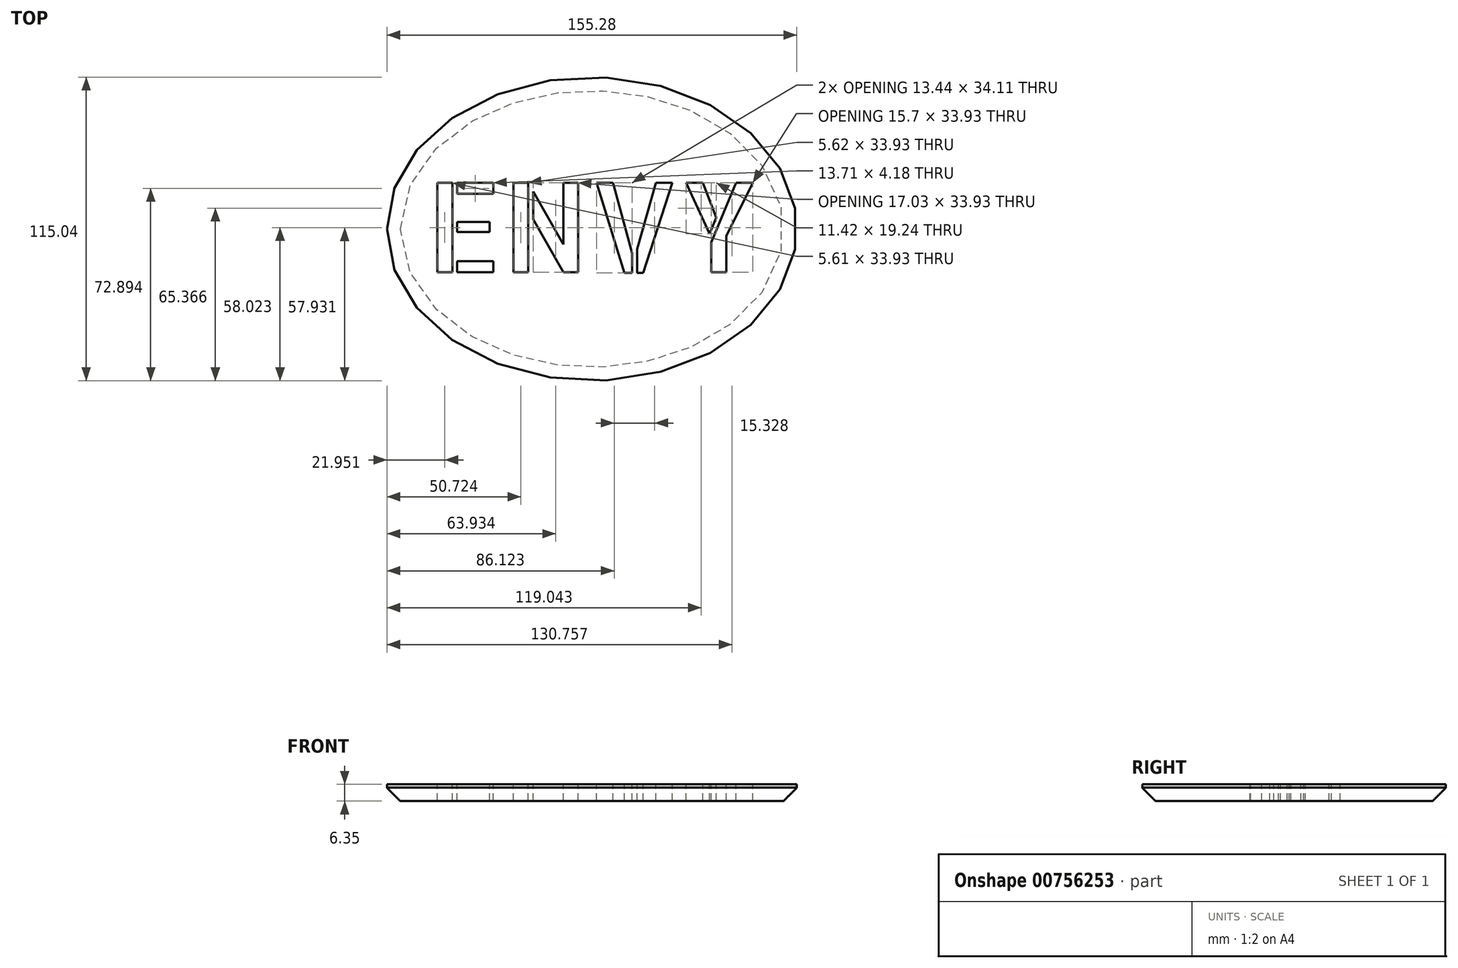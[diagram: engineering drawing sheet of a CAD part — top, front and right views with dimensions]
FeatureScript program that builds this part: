
annotation { "Feature Type Name" : "Feature", "Feature Type Description" : "" }
export const myFeature = defineFeature(function(context is Context, id is Id, definition is map)
    precondition{}
    {
        {
            var Q0;
            Q0=qCreatedBy(makeId("Top.planeOp"),FACE);
            var sketch = newSketch(context, id + "F0", { "sketchPlane" : qUnion([Q0])});
            skEllipse(sketch, "E0", {"center": v(0, 0) * mm, "majorRadius": 77.64 * mm, "minorRadius": 57.52 * mm, "majorAxis": v(-1, 0)});
            skSolve(sketch);
        }
        {
            var Q0;
            Q0 = qSketchRegion(id + "F0", true);
            extrude(context, id + "F1", {"entities" : qUnion([Q0]), "depth" : 6.35 * mm, "offsetDistance" : 25.4 * mm});
        }
        {
            var Q0;
            Q0=makeQuery(id+"F1.opExtrude","CAP_EDGE",EDGE,{"disambiguationData":[OSD([sQuery(id+"F0.wireOp",EDGE,"E0")])],"isStart":true});
            chamfer(context, id + "F2", {"entities" : qUnion([Q0]), "width" : 5.08 * mm, "tangentPropagation" : true});
        }
        {
            var Q0;
            Q0=makeQuery(id+"F1.opExtrude","CAP_FACE",FACE,{"disambiguationData":[OSD([sQuery(id+"F0.wireOp",EDGE,"E0")])],"isStart":false});
            var sketch = newSketch(context, id + "F3", { "sketchPlane" : qUnion([Q0])});
            skText(sketch, "E1", { "text": "ENVY", "fontName": "AllertaStencil-Regular.ttf"});
            const initialGuessF3  = {"E1": [-0.06287, -0.01646, 1, 0, 0.03394]};
            skSetInitialGuess(sketch, initialGuessF3);
            skSolve(sketch);
        }
        {
            var Q0;
            Q0 = qSketchRegion(id + "F3", true);
            extrude(context, id + "F4", {"entities" : qUnion([Q0]), "operationType" : NewBodyOperationType.REMOVE, "oppositeDirection" : true, "depth" : 25.4 * mm, "offsetDistance" : 25.4 * mm});
        }
    });
